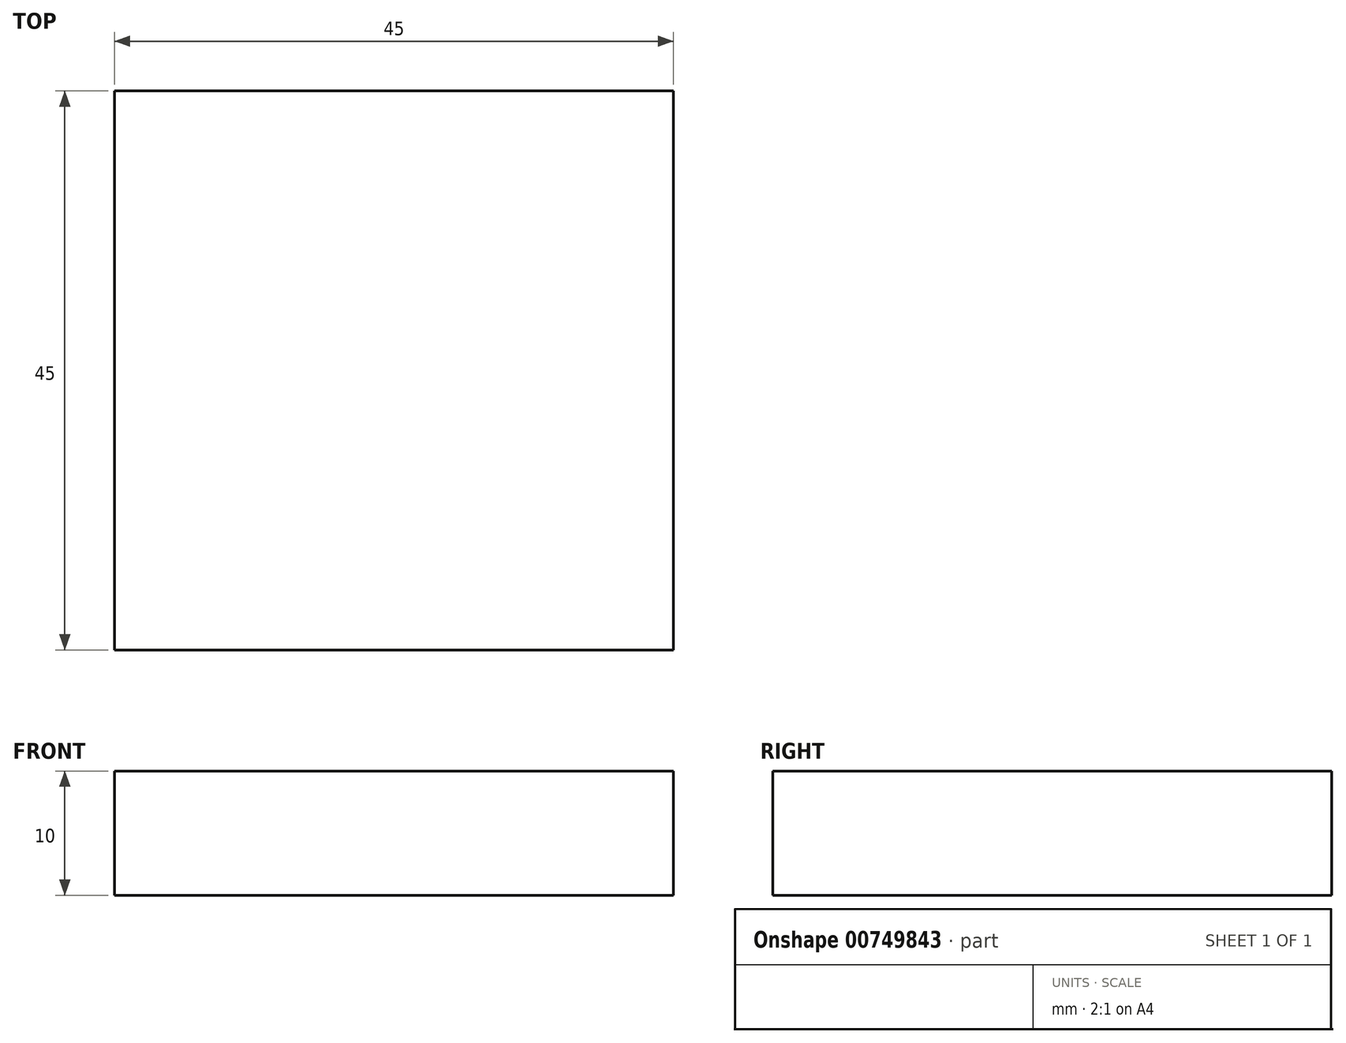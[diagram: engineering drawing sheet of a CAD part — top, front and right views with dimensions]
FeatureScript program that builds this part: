
annotation { "Feature Type Name" : "Feature", "Feature Type Description" : "" }
export const myFeature = defineFeature(function(context is Context, id is Id, definition is map)
    precondition{}
    {
        {
            var Q0;
            Q0=qCreatedBy(makeId("Top.planeOp"),FACE);
            var sketch = newSketch(context, id + "F0", { "sketchPlane" : qUnion([Q0])});
            skLineSegment(sketch, "E0.bottom", {"start": v(-16, 28.7) * mm, "end": v(29, 28.7) * mm});
            skLineSegment(sketch, "E0.top", {"start": v(-16, -16.3) * mm, "end": v(29, -16.3) * mm});
            skLineSegment(sketch, "E0.left", {"start": v(-16, 28.7) * mm, "end": v(-16, -16.3) * mm});
            skLineSegment(sketch, "E0.right", {"start": v(29, 28.7) * mm, "end": v(29, -16.3) * mm});
            skSolve(sketch);
        }
        {
            var Q0;
            Q0=makeQuery(id+"F0.imprint","IMPRINT",FACE,{"disambiguationData":[TD([[makeQuery(id+"F0.imprint","IMPRINT",EDGE,{"derivedFrom":sQuery(id+"F0.wireOp",EDGE,"E0.bottom")}),-1.0]])]});
            extrude(context, id + "F1", {"entities" : qUnion([Q0]), "depth" : 10 * mm, "offsetDistance" : 25 * mm});
        }
    });
